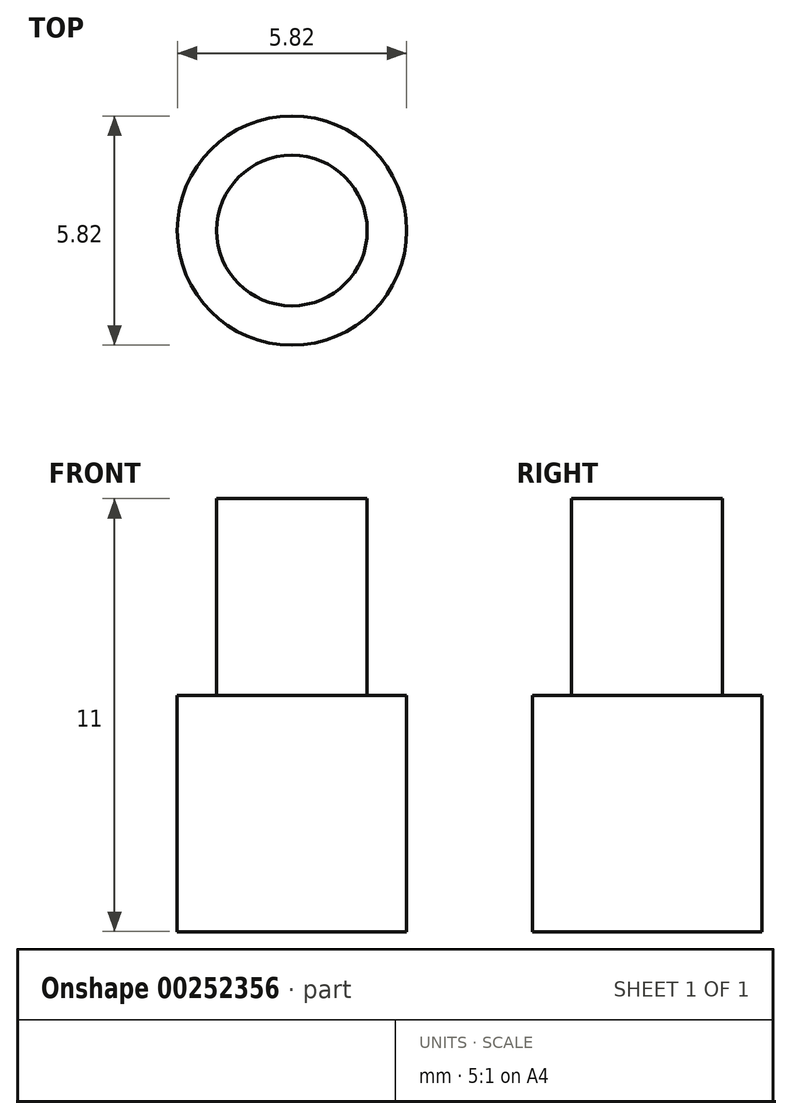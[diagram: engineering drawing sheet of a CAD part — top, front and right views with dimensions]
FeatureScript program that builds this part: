
annotation { "Feature Type Name" : "Feature", "Feature Type Description" : "" }
export const myFeature = defineFeature(function(context is Context, id is Id, definition is map)
    precondition{}
    {
        {
            var Q0;
            Q0=qCreatedBy(makeId("Front.planeOp"),FACE);
            var sketch = newSketch(context, id + "F0", { "sketchPlane" : qUnion([Q0])});
            skLineSegment(sketch, "E0.bottom", {"start": v(-1.25, 1.57) * mm, "end": v(5.66, 1.57) * mm});
            skLineSegment(sketch, "E0.top", {"start": v(-1.25, -4.43) * mm, "end": v(5.66, -4.43) * mm});
            skLineSegment(sketch, "E0.left", {"start": v(-1.25, 1.57) * mm, "end": v(-1.25, -4.43) * mm});
            skLineSegment(sketch, "E0.right", {"start": v(5.66, 1.57) * mm, "end": v(5.66, -4.43) * mm});
            skLineSegment(sketch, "E1", {"start": v(1.66, 1.57) * mm, "end": v(1.66, -4.43) * mm});
            skPoint(sketch, "E1.endSnap0", {"position": v(2.2, -4.43) * mm});
            skSolve(sketch);
        }
        {
            var Q0;
            {var subQ0=sQuery(id+"F0.wireOp",EDGE,"E0.left");Q0=makeQuery(id+"F0.imprint","IMPRINT",FACE,{"disambiguationData":[TD([[makeQuery(id+"F0.imprint","IMPRINT",EDGE,{"derivedFrom":subQ0}),1.0]])]});}
            var Q1;
            Q1=sQuery(id+"F0.wireOp",EDGE,"E1");
            revolve(context, id + "F1", {"entities" : qUnion([Q0]), "axis" : qUnion([Q1]), "revolveType" : RevolveType.FULL});
        }
        {
            var Q0;
            Q0=makeQuery(id+"F1.opRevolve","SWEPT_FACE",FACE,{"disambiguationData":[OSD([sQuery(id+"F0.wireOp",EDGE,"E0.bottom")])]});
            shell(context, id + "F2", {"entities" : qUnion([Q0]), "thickness" : 1 * mm});
        }
        {
            var Q0;
            Q0=makeQuery(id+"F2.opShell","OFFSET_FACE",FACE,{"disambiguationData":[OSD([sQuery(id+"F0.wireOp",EDGE,"E0.top")])]});
            extrude(context, id + "F3", {"entities" : qUnion([Q0]), "operationType" : NewBodyOperationType.ADD, "depth" : 10 * mm});
        }
    });
